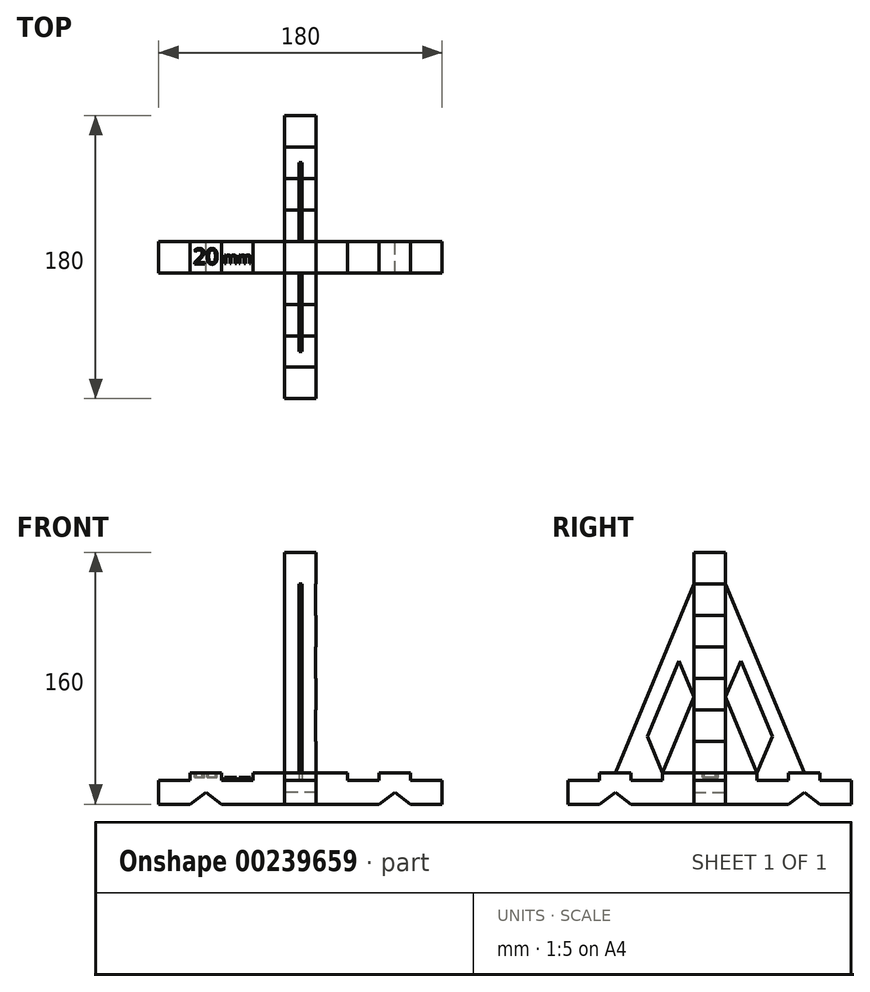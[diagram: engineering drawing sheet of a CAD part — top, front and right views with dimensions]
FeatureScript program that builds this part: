
annotation { "Feature Type Name" : "Feature", "Feature Type Description" : "" }
export const myFeature = defineFeature(function(context is Context, id is Id, definition is map)
    precondition{}
    {
        {
            var Q0;
            Q0=qCreatedBy(makeId("Top.planeOp"),FACE);
            var sketch = newSketch(context, id + "F0", { "sketchPlane" : qUnion([Q0])});
            skLineSegment(sketch, "E0.bottom", {"start": v(0, 0) * mm, "end": v(20, 0) * mm});
            skLineSegment(sketch, "E0.top", {"start": v(0, -20) * mm, "end": v(20, -20) * mm});
            skLineSegment(sketch, "E0.left", {"start": v(0, 0) * mm, "end": v(0, -20) * mm});
            skLineSegment(sketch, "E0.right", {"start": v(20, 0) * mm, "end": v(20, -20) * mm});
            skSolve(sketch);
        }
        {
            var Q0;
            Q0=makeQuery(id+"F0.imprint","IMPRINT",FACE,{"disambiguationData":[TD([[makeQuery(id+"F0.imprint","IMPRINT",EDGE,{"derivedFrom":sQuery(id+"F0.wireOp",EDGE,"E0.bottom")}),-1.0]])]});
            extrude(context, id + "F1", {"entities" : qUnion([Q0]), "depth" : 160 * mm});
        }
        {
            var Q0;
            Q0=makeQuery(id+"F1.opExtrude","SWEPT_FACE",FACE,{"disambiguationData":[OSD([sQuery(id+"F0.wireOp",EDGE,"E0.right")])]});
            var sketch = newSketch(context, id + "F2", { "sketchPlane" : qUnion([Q0])});
            skLineSegment(sketch, "E1.bottom", {"start": v(-20, 0) * mm, "end": v(0, 0) * mm});
            skLineSegment(sketch, "E1.top", {"start": v(-20, 20) * mm, "end": v(0, 20) * mm});
            skLineSegment(sketch, "E1.left", {"start": v(-20, 0) * mm, "end": v(-20, 20) * mm});
            skLineSegment(sketch, "E1.right", {"start": v(0, 0) * mm, "end": v(0, 20) * mm});
            skSolve(sketch);
        }
        {
            var Q0;
            Q0 = qSketchRegion(id + "F2", true);
            extrude(context, id + "F3", {"entities" : qUnion([Q0]), "operationType" : NewBodyOperationType.ADD, "depth" : 80 * mm, "hasSecondDirection" : true, "secondDirectionOppositeDirection" : true, "secondDirectionDepth" : 100 * mm});
        }
        {
            var Q0;
            Q0=makeQuery(id+"F3.boolean.opBoolean","MERGE",FACE,{"derivedFrom":[makeQuery(id+"F1.opExtrude","SWEPT_FACE",FACE,{"disambiguationData":[OSD([sQuery(id+"F0.wireOp",EDGE,"E0.top")])]}),makeQuery(id+"F3.opExtrude","SWEPT_FACE",FACE,{"disambiguationData":[OSD([sQuery(id+"F2.wireOp",EDGE,"E1.left")])]})]});
            var sketch = newSketch(context, id + "F4", { "sketchPlane" : qUnion([Q0])});
            skLineSegment(sketch, "E2.bottom", {"start": v(0, 20) * mm, "end": v(20, 20) * mm});
            skLineSegment(sketch, "E2.top", {"start": v(0, 0) * mm, "end": v(20, 0) * mm});
            skLineSegment(sketch, "E2.left", {"start": v(0, 20) * mm, "end": v(0, 0) * mm});
            skLineSegment(sketch, "E2.right", {"start": v(20, 20) * mm, "end": v(20, 0) * mm});
            skSolve(sketch);
        }
        {
            var Q0;
            Q0 = qSketchRegion(id + "F4", true);
            extrude(context, id + "F5", {"entities" : qUnion([Q0]), "operationType" : NewBodyOperationType.ADD, "depth" : 80 * mm, "hasSecondDirection" : true, "secondDirectionOppositeDirection" : true, "secondDirectionDepth" : 100 * mm});
        }
        {
            var Q0;
            {var subQ1=sQuery(id+"F2.wireOp",EDGE,"E1.left");var subQ2=sQuery(id+"F2.wireOp",EDGE,"E1.top");var subQ3=sQuery(id+"F2.wireOp",EDGE,"E1.bottom");var subQ4=sQuery(id+"F0.wireOp",EDGE,"E0.top");var subQ5=makeQuery(id+"F1.opExtrude","SWEPT_FACE",FACE,{"disambiguationData":[OSD([subQ4])]});var subQ6=makeQuery(id+"F3.opExtrude","SWEPT_FACE",FACE,{"disambiguationData":[OSD([subQ1])]});Q0=makeQuery(id+"F5.boolean.opBoolean","SPLIT",FACE,{"disambiguationData":[TD([makeQuery(id+"F3.opExtrude","CAP_FACE",FACE,{"disambiguationData":[OSD([subQ3,subQ2,subQ1,sQuery(id+"F2.wireOp",EDGE,"E1.right")])],"isStart":true})])],"derivedFrom":makeQuery(id+"F3.boolean.opBoolean","MERGE",FACE,{"derivedFrom":[subQ5,subQ6]})});}
            var sketch = newSketch(context, id + "F6", { "sketchPlane" : qUnion([Q0])});
            skLineSegment(sketch, "E3", {"start": v(0, 20) * mm, "end": v(-20, 20) * mm});
            skLineSegment(sketch, "E4", {"start": v(-20, 20) * mm, "end": v(-20, 15) * mm});
            skLineSegment(sketch, "E5", {"start": v(-20, 15) * mm, "end": v(-40, 15) * mm});
            skLineSegment(sketch, "E6", {"start": v(-40, 15) * mm, "end": v(-40, 20) * mm});
            skLineSegment(sketch, "E7", {"start": v(-40, 20) * mm, "end": v(-60, 20) * mm});
            skLineSegment(sketch, "E8", {"start": v(-60, 20) * mm, "end": v(-60, 15) * mm});
            skLineSegment(sketch, "E9", {"start": v(-60, 15) * mm, "end": v(-80, 15) * mm});
            skLineSegment(sketch, "E10", {"start": v(-80, 15) * mm, "end": v(-80, 26.1) * mm});
            skLineSegment(sketch, "E11", {"start": v(-80, 26.1) * mm, "end": v(-20, 26.1) * mm});
            skLineSegment(sketch, "E12", {"start": v(-20, 26.1) * mm, "end": v(-20, 20) * mm});
            skLineSegment(sketch, "E13.0", {"start": v(100, 20) * mm, "end": v(20, 20) * mm});
            skLineSegment(sketch, "E14", {"start": v(20, 20) * mm, "end": v(40, 20) * mm});
            skLineSegment(sketch, "E15", {"start": v(40, 20) * mm, "end": v(40, 15) * mm});
            skLineSegment(sketch, "E16", {"start": v(40, 15) * mm, "end": v(60, 15) * mm});
            skLineSegment(sketch, "E17", {"start": v(60, 15) * mm, "end": v(60, 20) * mm});
            skLineSegment(sketch, "E18", {"start": v(60, 20) * mm, "end": v(80, 20) * mm});
            skLineSegment(sketch, "E19", {"start": v(80, 20) * mm, "end": v(80, 15) * mm});
            skLineSegment(sketch, "E20", {"start": v(80, 15) * mm, "end": v(100, 15) * mm});
            skLineSegment(sketch, "E21", {"start": v(100, 15) * mm, "end": v(100, 26.33) * mm});
            skLineSegment(sketch, "E22", {"start": v(100, 26.33) * mm, "end": v(40, 26.33) * mm});
            skLineSegment(sketch, "E23", {"start": v(40, 26.33) * mm, "end": v(40, 20) * mm});
            skLineSegment(sketch, "E24", {"start": v(20, 20) * mm, "end": v(20, 40) * mm});
            skLineSegment(sketch, "E25", {"start": v(20, 40) * mm, "end": v(19.5, 40) * mm});
            skLineSegment(sketch, "E26", {"start": v(19.5, 40) * mm, "end": v(19.5, 60) * mm});
            skLineSegment(sketch, "E27", {"start": v(19.5, 60) * mm, "end": v(20, 60) * mm});
            skLineSegment(sketch, "E28", {"start": v(20, 60) * mm, "end": v(20, 80) * mm});
            skLineSegment(sketch, "E29", {"start": v(20, 80) * mm, "end": v(19.5, 80) * mm});
            skLineSegment(sketch, "E30", {"start": v(19.5, 80) * mm, "end": v(19.5, 100) * mm});
            skLineSegment(sketch, "E31", {"start": v(19.5, 100) * mm, "end": v(20, 100) * mm});
            skLineSegment(sketch, "E32", {"start": v(20, 100) * mm, "end": v(20, 120) * mm});
            skLineSegment(sketch, "E33", {"start": v(20, 120) * mm, "end": v(19.5, 120) * mm});
            skLineSegment(sketch, "E34", {"start": v(19.5, 120) * mm, "end": v(19.5, 140) * mm});
            skLineSegment(sketch, "E35", {"start": v(19.5, 140) * mm, "end": v(20, 140) * mm});
            skLineSegment(sketch, "E36.0", {"start": v(20, 160) * mm, "end": v(20, 20) * mm});
            skLineSegment(sketch, "E37", {"start": v(20, 140) * mm, "end": v(20, 160) * mm});
            skSolve(sketch);
        }
        {
            var Q0;
            {var subQ0=sQuery(id+"F6.wireOp",EDGE,"E8");Q0=makeQuery(id+"F6.imprint","IMPRINT",FACE,{"disambiguationData":[TD([[makeQuery(id+"F6.imprint","IMPRINT",EDGE,{"derivedFrom":subQ0}),-1.0]])]});}
            var Q1;
            {var subQ0=sQuery(id+"F6.wireOp",EDGE,"E4");Q1=makeQuery(id+"F6.imprint","IMPRINT",FACE,{"disambiguationData":[TD([[makeQuery(id+"F6.imprint","IMPRINT",EDGE,{"derivedFrom":subQ0}),-1.0]])]});}
            var Q2;
            {var subQ0=sQuery(id+"F6.wireOp",EDGE,"E15");Q2=makeQuery(id+"F6.imprint","IMPRINT",FACE,{"disambiguationData":[TD([[makeQuery(id+"F6.imprint","IMPRINT",EDGE,{"derivedFrom":subQ0}),1.0]])]});}
            var Q3;
            {var subQ3=sQuery(id+"F6.wireOp",EDGE,"E19");Q3=makeQuery(id+"F6.imprint","IMPRINT",FACE,{"disambiguationData":[TD([[makeQuery(id+"F6.imprint","IMPRINT",EDGE,{"derivedFrom":subQ3}),1.0]])]});}
            var Q4;
            {var subQ0=sQuery(id+"F6.wireOp",EDGE,"E25");Q4=makeQuery(id+"F6.imprint","IMPRINT",FACE,{"disambiguationData":[TD([[makeQuery(id+"F6.imprint","IMPRINT",EDGE,{"derivedFrom":subQ0}),-1.0]])]});}
            var Q5;
            {var subQ0=sQuery(id+"F6.wireOp",EDGE,"E29");Q5=makeQuery(id+"F6.imprint","IMPRINT",FACE,{"disambiguationData":[TD([[makeQuery(id+"F6.imprint","IMPRINT",EDGE,{"derivedFrom":subQ0}),-1.0]])]});}
            var Q6;
            {var subQ0=sQuery(id+"F6.wireOp",EDGE,"E33");Q6=makeQuery(id+"F6.imprint","IMPRINT",FACE,{"disambiguationData":[TD([[makeQuery(id+"F6.imprint","IMPRINT",EDGE,{"derivedFrom":subQ0}),-1.0]])]});}
            extrude(context, id + "F7", {"entities" : qUnion([Q0, Q1, Q2, Q3, Q4, Q5, Q6]), "operationType" : NewBodyOperationType.REMOVE, "oppositeDirection" : true, "depth" : 25 * mm});
        }
        {
            var Q0;
            {var subQ1=sQuery(id+"F0.wireOp",EDGE,"E0.top");var subQ3=sQuery(id+"F4.wireOp",EDGE,"E2.right");Q0=makeQuery(id+"F5.boolean.opBoolean","SPLIT",FACE,{"disambiguationData":[TD([makeQuery(id+"F1.opExtrude","SWEPT_FACE",FACE,{"disambiguationData":[OSD([subQ1])]})])],"derivedFrom":makeQuery(id+"F5.opExtrude","SWEPT_FACE",FACE,{"disambiguationData":[OSD([subQ3])]})});}
            var sketch = newSketch(context, id + "F8", { "sketchPlane" : qUnion([Q0])});
            skLineSegment(sketch, "E38", {"start": v(-20, 20) * mm, "end": v(-40, 20) * mm});
            skLineSegment(sketch, "E39", {"start": v(-40, 20) * mm, "end": v(-40, 15) * mm});
            skLineSegment(sketch, "E40", {"start": v(-40, 15) * mm, "end": v(-60, 15) * mm});
            skLineSegment(sketch, "E41", {"start": v(-60, 15) * mm, "end": v(-60, 20) * mm});
            skLineSegment(sketch, "E42", {"start": v(-60, 20) * mm, "end": v(-80, 20) * mm});
            skLineSegment(sketch, "E43", {"start": v(-80, 20) * mm, "end": v(-80, 15) * mm});
            skLineSegment(sketch, "E44", {"start": v(-80, 15) * mm, "end": v(-100, 15) * mm});
            skLineSegment(sketch, "E45", {"start": v(-100, 15) * mm, "end": v(-100, 20) * mm});
            skLineSegment(sketch, "E46", {"start": v(-100, 20) * mm, "end": v(-40, 20) * mm});
            skLineSegment(sketch, "E47", {"start": v(0, 20) * mm, "end": v(20, 20) * mm});
            skLineSegment(sketch, "E48", {"start": v(20, 20) * mm, "end": v(20, 15) * mm});
            skLineSegment(sketch, "E49", {"start": v(20, 15) * mm, "end": v(40, 15) * mm});
            skLineSegment(sketch, "E50", {"start": v(40, 15) * mm, "end": v(40, 20) * mm});
            skLineSegment(sketch, "E51", {"start": v(40, 20) * mm, "end": v(60, 20) * mm});
            skLineSegment(sketch, "E52", {"start": v(60, 20) * mm, "end": v(60, 15) * mm});
            skLineSegment(sketch, "E53.0", {"start": v(0, 20) * mm, "end": v(80, 20) * mm});
            skLineSegment(sketch, "E54", {"start": v(60, 15) * mm, "end": v(80, 15) * mm});
            skLineSegment(sketch, "E55", {"start": v(80, 15) * mm, "end": v(80, 20) * mm});
            skLineSegment(sketch, "E56", {"start": v(20, 20) * mm, "end": v(80, 20) * mm});
            skLineSegment(sketch, "E57", {"start": v(-80, 20) * mm, "end": v(-60, 20) * mm});
            skSolve(sketch);
        }
        {
            var Q0;
            Q0 = qSketchRegion(id + "F8", true);
            extrude(context, id + "F9", {"entities" : qUnion([Q0]), "operationType" : NewBodyOperationType.REMOVE, "oppositeDirection" : true, "depth" : 25 * mm});
        }
        {
            var Q0;
            Q0=makeQuery(id+"F1.opExtrude","SWEPT_FACE",FACE,{"disambiguationData":[OSD([sQuery(id+"F0.wireOp",EDGE,"E0.left")])]});
            cPlane(context, id + "F10", {"entities" : qUnion([Q0]), "cplaneType" : CPlaneType.OFFSET, "offset" : 10 * mm, "oppositeDirection" : true, "width" : 150 * mm, "height" : 150 * mm});
        }
        {
            var Q0;
            Q0=qCreatedBy(id+"F10.planeOp",FACE);
            var sketch = newSketch(context, id + "F11", { "sketchPlane" : qUnion([Q0])});
            skLineSegment(sketch, "E58.0.0", {"start": v(0, 160) * mm, "end": v(0, 20) * mm});
            skLineSegment(sketch, "E58.0.1", {"start": v(0, 20) * mm, "end": v(20, 20) * mm});
            skLineSegment(sketch, "E58.0.2", {"start": v(20, 20) * mm, "end": v(20, 160) * mm});
            skLineSegment(sketch, "E58.0.3", {"start": v(20, 160) * mm, "end": v(0, 160) * mm});
            skLineSegment(sketch, "E59.0.0", {"start": v(-40, 20) * mm, "end": v(-60, 20) * mm});
            skLineSegment(sketch, "E59.0.1", {"start": v(-60, 20) * mm, "end": v(-60, 15) * mm});
            skLineSegment(sketch, "E59.0.2", {"start": v(-60, 15) * mm, "end": v(-80, 15) * mm});
            skLineSegment(sketch, "E59.0.3", {"start": v(-80, 15) * mm, "end": v(-80, 0) * mm});
            skLineSegment(sketch, "E59.0.4", {"start": v(-80, 0) * mm, "end": v(0, 0) * mm});
            skLineSegment(sketch, "E59.0.5", {"start": v(0, 0) * mm, "end": v(0, 20) * mm});
            skLineSegment(sketch, "E59.0.6", {"start": v(0, 20) * mm, "end": v(-20, 20) * mm});
            skLineSegment(sketch, "E59.0.7", {"start": v(-20, 20) * mm, "end": v(-20, 15) * mm});
            skLineSegment(sketch, "E59.0.8", {"start": v(-20, 15) * mm, "end": v(-40, 15) * mm});
            skLineSegment(sketch, "E59.0.9", {"start": v(-40, 15) * mm, "end": v(-40, 20) * mm});
            skLineSegment(sketch, "E60.0.0", {"start": v(100, 15) * mm, "end": v(80, 15) * mm});
            skLineSegment(sketch, "E60.0.1", {"start": v(80, 15) * mm, "end": v(80, 20) * mm});
            skLineSegment(sketch, "E60.0.2", {"start": v(80, 20) * mm, "end": v(60, 20) * mm});
            skLineSegment(sketch, "E60.0.3", {"start": v(60, 20) * mm, "end": v(60, 15) * mm});
            skLineSegment(sketch, "E60.0.4", {"start": v(60, 15) * mm, "end": v(40, 15) * mm});
            skLineSegment(sketch, "E60.0.5", {"start": v(40, 15) * mm, "end": v(40, 20) * mm});
            skLineSegment(sketch, "E60.0.6", {"start": v(40, 20) * mm, "end": v(20, 20) * mm});
            skLineSegment(sketch, "E60.0.7", {"start": v(20, 20) * mm, "end": v(20, 0) * mm});
            skLineSegment(sketch, "E60.0.8", {"start": v(20, 0) * mm, "end": v(100, 0) * mm});
            skLineSegment(sketch, "E60.0.9", {"start": v(100, 0) * mm, "end": v(100, 15) * mm});
            skLineSegment(sketch, "E61", {"start": v(0, 140) * mm, "end": v(-50, 20) * mm});
            skLineSegment(sketch, "E62", {"start": v(20, 140) * mm, "end": v(70, 20) * mm});
            skLineSegment(sketch, "E63", {"start": v(-40, 20) * mm, "end": v(-30, 44) * mm});
            skLineSegment(sketch, "E64", {"start": v(-30, 44) * mm, "end": v(-20, 20) * mm});
            skLineSegment(sketch, "E65", {"start": v(40, 20) * mm, "end": v(50, 44) * mm});
            skLineSegment(sketch, "E66", {"start": v(50, 44) * mm, "end": v(60, 20) * mm});
            skLineSegment(sketch, "E67", {"start": v(-23.95, 58.53) * mm, "end": v(-7.9, 97.06) * mm});
            skLineSegment(sketch, "E68", {"start": v(-30, 44) * mm, "end": v(-23.95, 58.53) * mm, "construction": true});
            skLineSegment(sketch, "E69", {"start": v(-7.9, 97.06) * mm, "end": v(-7.9, 20) * mm});
            skLineSegment(sketch, "E70", {"start": v(-7.9, 20) * mm, "end": v(-23.95, 58.53) * mm});
            skLineSegment(sketch, "E71", {"start": v(50, 44) * mm, "end": v(44.16, 58.01) * mm, "construction": true});
            skLineSegment(sketch, "E72", {"start": v(44.16, 58.01) * mm, "end": v(28.32, 96.02) * mm});
            skLineSegment(sketch, "E73", {"start": v(28.32, 96.02) * mm, "end": v(28.32, 20) * mm});
            skLineSegment(sketch, "E74", {"start": v(28.32, 20) * mm, "end": v(44.16, 58.01) * mm});
            skSolve(sketch);
        }
        {
            var Q0;
            {var subQ9=sQuery(id+"F11.wireOp",EDGE,"E61");Q0=makeQuery(id+"F11.imprint","IMPRINT",FACE,{"disambiguationData":[TD([[makeQuery(id+"F11.imprint","IMPRINT",EDGE,{"derivedFrom":subQ9}),1.0]])]});}
            var Q1;
            {var subQ9=sQuery(id+"F11.wireOp",EDGE,"E62");Q1=makeQuery(id+"F11.imprint","IMPRINT",FACE,{"disambiguationData":[TD([[makeQuery(id+"F11.imprint","IMPRINT",EDGE,{"derivedFrom":subQ9}),-1.0]])]});}
            var Q2;
            Q2=makeQuery(id+"F11.imprint","IMPRINT",FACE,{"disambiguationData":[TD([[makeQuery(id+"F11.imprint","IMPRINT",EDGE,{"derivedFrom":sQuery(id+"F11.wireOp",EDGE,"E67")}),-1.0]])]});
            var Q3;
            Q3=makeQuery(id+"F11.imprint","IMPRINT",FACE,{"disambiguationData":[TD([[makeQuery(id+"F11.imprint","IMPRINT",EDGE,{"derivedFrom":sQuery(id+"F11.wireOp",EDGE,"E72")}),1.0]])]});
            var Q4;
            Q4=makeQuery(id+"F11.imprint","IMPRINT",FACE,{"disambiguationData":[TD([[makeQuery(id+"F11.imprint","IMPRINT",EDGE,{"derivedFrom":sQuery(id+"F11.wireOp",EDGE,"E60.0.3")}),-1.0]])]});
            var Q5;
            Q5=makeQuery(id+"F11.imprint","IMPRINT",FACE,{"disambiguationData":[TD([[makeQuery(id+"F11.imprint","IMPRINT",EDGE,{"derivedFrom":sQuery(id+"F11.wireOp",EDGE,"E59.0.7")}),-1.0]])]});
            extrude(context, id + "F12", {"entities" : qUnion([Q0, Q1, Q2, Q3, Q4, Q5]), "operationType" : NewBodyOperationType.ADD, "endBound" : BoundingType.SYMMETRIC, "depth" : 2 * mm});
        }
        {
            var Q0;
            {var subQ1=sQuery(id+"F2.wireOp",EDGE,"E1.bottom");var subQ2=sQuery(id+"F0.wireOp",EDGE,"E0.bottom");var subQ3=sQuery(id+"F2.wireOp",EDGE,"E1.right");var subQ4=makeQuery(id+"F3.opExtrude","SWEPT_FACE",FACE,{"disambiguationData":[OSD([subQ3])]});var subQ5=makeQuery(id+"F1.opExtrude","SWEPT_FACE",FACE,{"disambiguationData":[OSD([subQ2])]});var subQ6=sQuery(id+"F2.wireOp",EDGE,"E1.top");Q0=makeQuery(id+"F5.boolean.opBoolean","SPLIT",FACE,{"disambiguationData":[TD([makeQuery(id+"F3.opExtrude","CAP_FACE",FACE,{"disambiguationData":[OSD([subQ1,subQ6,sQuery(id+"F2.wireOp",EDGE,"E1.left"),subQ3])],"isStart":false})])],"derivedFrom":makeQuery(id+"F3.boolean.opBoolean","MERGE",FACE,{"derivedFrom":[subQ5,subQ4]})});}
            var sketch = newSketch(context, id + "F13", { "sketchPlane" : qUnion([Q0])});
            skLineSegment(sketch, "E75", {"start": v(-80, 0) * mm, "end": v(-70, 7.5) * mm});
            skPoint(sketch, "E75.endSnap0", {"position": v(-100, 7.5) * mm});
            skPoint(sketch, "E75.endSnap1", {"position": v(-70, 20) * mm});
            skLineSegment(sketch, "E76", {"start": v(-70, 7.5) * mm, "end": v(-60, 0) * mm});
            skLineSegment(sketch, "E77.0.0", {"start": v(80, 0) * mm, "end": v(80, 15) * mm});
            skLineSegment(sketch, "E77.0.1", {"start": v(80, 15) * mm, "end": v(60, 15) * mm});
            skLineSegment(sketch, "E77.0.2", {"start": v(60, 15) * mm, "end": v(60, 20) * mm});
            skLineSegment(sketch, "E77.0.3", {"start": v(60, 20) * mm, "end": v(40, 20) * mm});
            skLineSegment(sketch, "E77.0.4", {"start": v(40, 20) * mm, "end": v(40, 15) * mm});
            skLineSegment(sketch, "E77.0.5", {"start": v(40, 15) * mm, "end": v(20, 15) * mm});
            skLineSegment(sketch, "E77.0.6", {"start": v(20, 15) * mm, "end": v(20, 20) * mm});
            skLineSegment(sketch, "E77.0.7", {"start": v(20, 20) * mm, "end": v(0, 20) * mm});
            skLineSegment(sketch, "E77.0.8", {"start": v(0, 20) * mm, "end": v(0, 0) * mm});
            skLineSegment(sketch, "E77.0.9", {"start": v(0, 0) * mm, "end": v(80, 0) * mm});
            skLineSegment(sketch, "E78", {"start": v(60, 0) * mm, "end": v(50, 7.5) * mm});
            skPoint(sketch, "E78.endSnap0", {"position": v(50, 20) * mm});
            skPoint(sketch, "E78.endSnap1", {"position": v(80, 7.5) * mm});
            skLineSegment(sketch, "E79", {"start": v(50, 7.5) * mm, "end": v(40, 0) * mm});
            skSolve(sketch);
        }
        {
            var Q0;
            {var subQ0=sQuery(id+"F13.wireOp",EDGE,"E75");Q0=makeQuery(id+"F13.imprint","IMPRINT",FACE,{"disambiguationData":[TD([[makeQuery(id+"F13.imprint","IMPRINT",EDGE,{"derivedFrom":subQ0}),-1.0]])]});}
            var Q1;
            {var subQ0=sQuery(id+"F13.wireOp",EDGE,"E78");Q1=makeQuery(id+"F13.imprint","IMPRINT",FACE,{"disambiguationData":[TD([[makeQuery(id+"F13.imprint","IMPRINT",EDGE,{"derivedFrom":subQ0}),1.0]])]});}
            extrude(context, id + "F14", {"entities" : qUnion([Q0, Q1]), "operationType" : NewBodyOperationType.REMOVE, "oppositeDirection" : true, "depth" : 25 * mm});
        }
        {
            var Q0;
            {var subQ1=sQuery(id+"F0.wireOp",EDGE,"E0.bottom");var subQ3=sQuery(id+"F4.wireOp",EDGE,"E2.left");Q0=makeQuery(id+"F5.boolean.opBoolean","SPLIT",FACE,{"disambiguationData":[TD([makeQuery(id+"F1.opExtrude","SWEPT_FACE",FACE,{"disambiguationData":[OSD([subQ1])]})])],"derivedFrom":makeQuery(id+"F5.opExtrude","SWEPT_FACE",FACE,{"disambiguationData":[OSD([subQ3])]})});}
            var sketch = newSketch(context, id + "F15", { "sketchPlane" : qUnion([Q0])});
            skLineSegment(sketch, "E80", {"start": v(-60, 0) * mm, "end": v(-50, 7.5) * mm});
            skPoint(sketch, "E80.endSnap0", {"position": v(-50, 20) * mm});
            skPoint(sketch, "E80.endSnap1", {"position": v(-80, 7.5) * mm});
            skLineSegment(sketch, "E81", {"start": v(-50, 7.5) * mm, "end": v(-40, 0) * mm});
            skLineSegment(sketch, "E82.0.0", {"start": v(100, 15) * mm, "end": v(80, 15) * mm});
            skLineSegment(sketch, "E82.0.1", {"start": v(80, 15) * mm, "end": v(80, 20) * mm});
            skLineSegment(sketch, "E82.0.2", {"start": v(80, 20) * mm, "end": v(60, 20) * mm});
            skLineSegment(sketch, "E82.0.3", {"start": v(60, 20) * mm, "end": v(60, 15) * mm});
            skLineSegment(sketch, "E82.0.4", {"start": v(60, 15) * mm, "end": v(40, 15) * mm});
            skLineSegment(sketch, "E82.0.5", {"start": v(40, 15) * mm, "end": v(40, 20) * mm});
            skLineSegment(sketch, "E82.0.6", {"start": v(40, 20) * mm, "end": v(20, 20) * mm});
            skLineSegment(sketch, "E82.0.7", {"start": v(20, 20) * mm, "end": v(20, 0) * mm});
            skLineSegment(sketch, "E82.0.8", {"start": v(20, 0) * mm, "end": v(100, 0) * mm});
            skLineSegment(sketch, "E82.0.9", {"start": v(100, 0) * mm, "end": v(100, 15) * mm});
            skLineSegment(sketch, "E83", {"start": v(80, 0) * mm, "end": v(70, 7.5) * mm});
            skPoint(sketch, "E83.endSnap0", {"position": v(100, 7.5) * mm});
            skPoint(sketch, "E83.endSnap1", {"position": v(70, 20) * mm});
            skLineSegment(sketch, "E84", {"start": v(70, 7.5) * mm, "end": v(60, 0) * mm});
            skSolve(sketch);
        }
        {
            var Q0;
            {var subQ0=sQuery(id+"F15.wireOp",EDGE,"E80");Q0=makeQuery(id+"F15.imprint","IMPRINT",FACE,{"disambiguationData":[TD([[makeQuery(id+"F15.imprint","IMPRINT",EDGE,{"derivedFrom":subQ0}),-1.0]])]});}
            var Q1;
            {var subQ0=sQuery(id+"F15.wireOp",EDGE,"E83");Q1=makeQuery(id+"F15.imprint","IMPRINT",FACE,{"disambiguationData":[TD([[makeQuery(id+"F15.imprint","IMPRINT",EDGE,{"derivedFrom":subQ0}),1.0]])]});}
            extrude(context, id + "F16", {"entities" : qUnion([Q0, Q1]), "operationType" : NewBodyOperationType.REMOVE, "oppositeDirection" : true, "depth" : 25 * mm});
        }
        {
            var Q0;
            Q0=makeQuery(id+"F12.opExtrude","CAP_FACE",FACE,{"disambiguationData":[OSD([sQuery(id+"F11.wireOp",EDGE,"E58.0.0"),sQuery(id+"F11.wireOp",EDGE,"E59.0.0"),sQuery(id+"F11.wireOp",EDGE,"E59.0.6"),sQuery(id+"F11.wireOp",EDGE,"E59.0.7"),sQuery(id+"F11.wireOp",EDGE,"E59.0.8"),sQuery(id+"F11.wireOp",EDGE,"E59.0.9"),sQuery(id+"F11.wireOp",EDGE,"E61")])],"isStart":false});
            var sketch = newSketch(context, id + "F17", { "sketchPlane" : qUnion([Q0])});
            skLineSegment(sketch, "E85", {"start": v(-20, 20) * mm, "end": v(-29.58, 43) * mm});
            skLineSegment(sketch, "E86", {"start": v(-29.58, 43) * mm, "end": v(-9.58, 91) * mm});
            skLineSegment(sketch, "E87", {"start": v(-9.58, 91) * mm, "end": v(0, 68) * mm});
            skLineSegment(sketch, "E88", {"start": v(0, 68) * mm, "end": v(-20, 20) * mm});
            skLineSegment(sketch, "E89.0.0", {"start": v(0, 160) * mm, "end": v(0, 20) * mm, "construction": true});
            skLineSegment(sketch, "E89.0.1", {"start": v(0, 20) * mm, "end": v(20, 20) * mm, "construction": true});
            skLineSegment(sketch, "E89.0.2", {"start": v(20, 20) * mm, "end": v(20, 160) * mm, "construction": true});
            skLineSegment(sketch, "E89.0.3", {"start": v(20, 160) * mm, "end": v(0, 160) * mm, "construction": true});
            skLineSegment(sketch, "E90", {"start": v(10, 20) * mm, "end": v(10, 126.81) * mm, "construction": true});
            skLineSegment(sketch, "E91.MirrorCS", {"start": v(29.58, 91) * mm, "end": v(20, 68) * mm});
            skLineSegment(sketch, "E92.MirrorCS", {"start": v(49.58, 43) * mm, "end": v(29.58, 91) * mm});
            skLineSegment(sketch, "E93.MirrorCS", {"start": v(20, 68) * mm, "end": v(40, 20) * mm});
            skLineSegment(sketch, "E94.MirrorCS", {"start": v(40, 20) * mm, "end": v(49.58, 43) * mm});
            skSolve(sketch);
        }
        {
            var Q0;
            Q0 = qSketchRegion(id + "F17", true);
            extrude(context, id + "F18", {"entities" : qUnion([Q0]), "operationType" : NewBodyOperationType.REMOVE, "oppositeDirection" : true, "depth" : 25 * mm});
        }
        {
            var Q0;
            {var subQ6=sQuery(id+"F2.wireOp",EDGE,"E1.top");Q0=makeQuery(id+"F7.boolean.opBoolean","SPLIT",FACE,{"disambiguationData":[TD([makeQuery(id+"F7.opExtrude","SWEPT_FACE",FACE,{"disambiguationData":[OSD([sQuery(id+"F6.wireOp",EDGE,"E6")])]})])],"derivedFrom":makeQuery(id+"F3.boolean.opBoolean","SPLIT",FACE,{"disambiguationData":[TD([makeQuery(id+"F1.opExtrude","SWEPT_FACE",FACE,{"disambiguationData":[OSD([sQuery(id+"F0.wireOp",EDGE,"E0.left")])]})])],"derivedFrom":makeQuery(id+"F3.opExtrude","SWEPT_FACE",FACE,{"disambiguationData":[OSD([subQ6])]})})});}
            var sketch = newSketch(context, id + "F19", { "sketchPlane" : qUnion([Q0])});
            skLineSegment(sketch, "E95.0", {"start": v(-42, -2) * mm, "end": v(-58, -2) * mm});
            skLineSegment(sketch, "E95.1", {"start": v(-42, -2) * mm, "end": v(-42, -18) * mm});
            skLineSegment(sketch, "E95.2", {"start": v(-42, -18) * mm, "end": v(-58, -18) * mm});
            skLineSegment(sketch, "E95.3", {"start": v(-58, -2) * mm, "end": v(-58, -18) * mm});
            skText(sketch, "E96", { "text": "20", "fontName": "OpenSans-Regular.ttf"});
            const initialGuessF19  = {"E96": [-0.058, -0.01447, 1, 0, 0.00994]};
            skSetInitialGuess(sketch, initialGuessF19);
            skSolve(sketch);
        }
        {
            var Q0;
            Q0=makeQuery(id+"F7.boolean.opBoolean","COPY",FACE,{"derivedFrom":makeQuery(id+"F7.opExtrude","SWEPT_FACE",FACE,{"disambiguationData":[OSD([sQuery(id+"F6.wireOp",EDGE,"E5")])]})});
            var sketch = newSketch(context, id + "F20", { "sketchPlane" : qUnion([Q0])});
            skText(sketch, "E97", { "text": "mm", "fontName": "OpenSans-Regular.ttf"});
            const initialGuessF20  = {"E97": [-0.039, -0.014, 1, 0, 0.00703]};
            skSetInitialGuess(sketch, initialGuessF20);
            skSolve(sketch);
        }
        {
            var Q0;
            Q0=makeQuery(id+"F19.imprint","IMPRINT",FACE,{"disambiguationData":[TD([[makeQuery(id+"F19.imprint","IMPRINT",EDGE,{"derivedFrom":sQuery(id+"F19.wireOp",EDGE,"E96.sketch_text.stroke-20")}),-1.0]])]});
            var Q1;
            Q1=makeQuery(id+"F19.imprint","IMPRINT",FACE,{"disambiguationData":[TD([[makeQuery(id+"F19.imprint","IMPRINT",EDGE,{"derivedFrom":sQuery(id+"F19.wireOp",EDGE,"E96.sketch_text.stroke-0")}),-1.0]])]});
            extrude(context, id + "F21", {"entities" : qUnion([Q0, Q1]), "operationType" : NewBodyOperationType.REMOVE, "oppositeDirection" : true, "depth" : 3 * mm});
        }
        {
            var Q0;
            Q0 = qSketchRegion(id + "F20", true);
            extrude(context, id + "F22", {"entities" : qUnion([Q0]), "operationType" : NewBodyOperationType.ADD, "depth" : 2 * mm});
        }
    });
